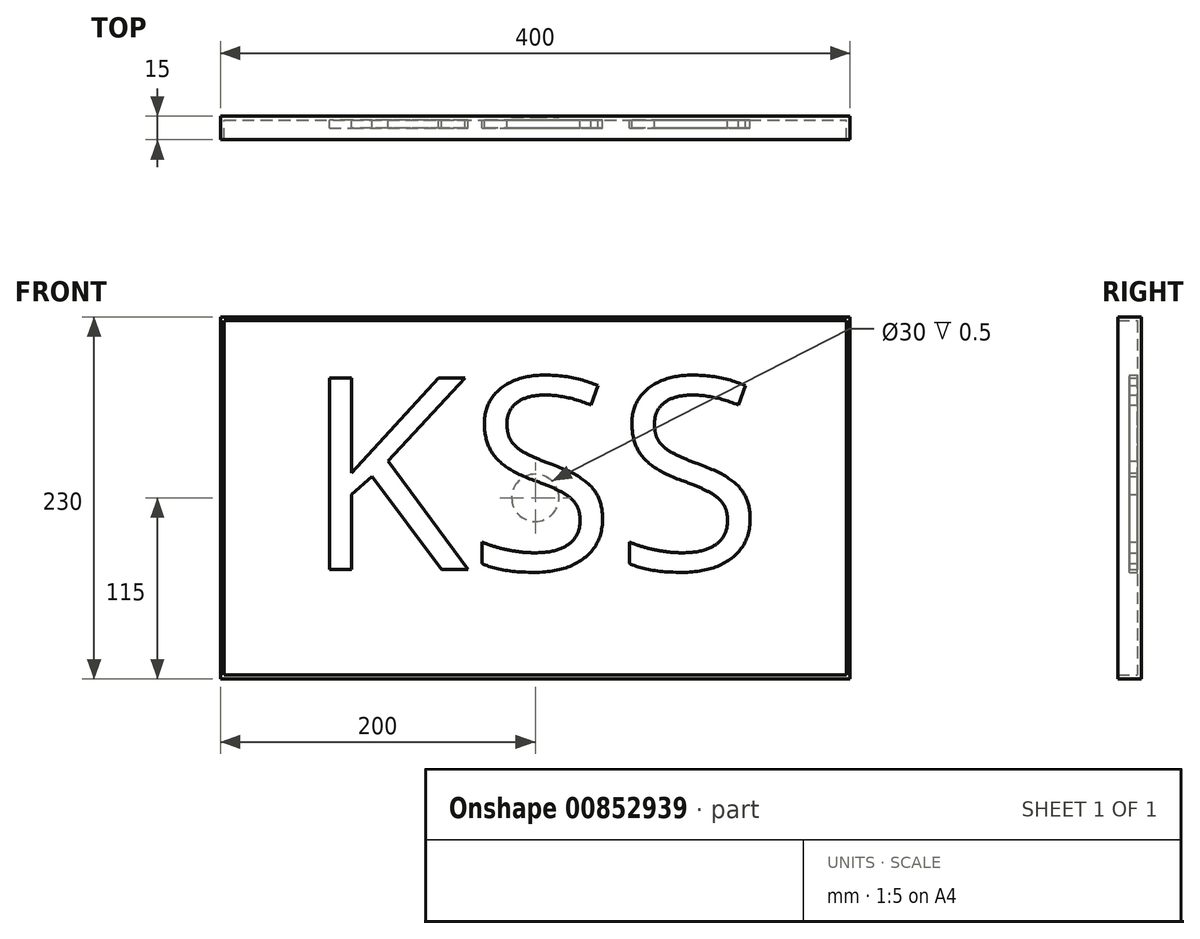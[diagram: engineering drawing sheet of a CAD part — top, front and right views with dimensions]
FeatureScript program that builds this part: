
annotation { "Feature Type Name" : "Feature", "Feature Type Description" : "" }
export const myFeature = defineFeature(function(context is Context, id is Id, definition is map)
    precondition{}
    {
        {
            var Q0;
            Q0=qCreatedBy(makeId("Front.planeOp"),FACE);
            var sketch = newSketch(context, id + "F0", { "sketchPlane" : qUnion([Q0])});
            skLineSegment(sketch, "E0.bottom", {"start": v(-200, 115) * mm, "end": v(200, 115) * mm});
            skLineSegment(sketch, "E0.top", {"start": v(-200, -115) * mm, "end": v(200, -115) * mm});
            skLineSegment(sketch, "E0.left", {"start": v(-200, 115) * mm, "end": v(-200, -115) * mm});
            skLineSegment(sketch, "E0.right", {"start": v(200, 115) * mm, "end": v(200, -115) * mm});
            skSolve(sketch);
        }
        {
            var Q0;
            Q0=makeQuery(id+"F0.imprint","IMPRINT",FACE,{"disambiguationData":[TD([[makeQuery(id+"F0.imprint","IMPRINT",EDGE,{"derivedFrom":sQuery(id+"F0.wireOp",EDGE,"E0.bottom")}),-1.0]])]});
            extrude(context, id + "F1", {"entities" : qUnion([Q0]), "depth" : 15 * mm, "offsetDistance" : 25 * mm});
        }
        {
            var Q0;
            Q0=makeQuery(id+"F1.opExtrude","CAP_FACE",FACE,{"disambiguationData":[OSD([sQuery(id+"F0.wireOp",EDGE,"E0.bottom"),sQuery(id+"F0.wireOp",EDGE,"E0.top"),sQuery(id+"F0.wireOp",EDGE,"E0.left"),sQuery(id+"F0.wireOp",EDGE,"E0.right")])],"isStart":false});
            shell(context, id + "F2", {"entities" : qUnion([Q0]), "thickness" : 2.5 * mm});
        }
        {
            var Q0;
            Q0=makeQuery(id+"F1.opExtrude","CAP_FACE",FACE,{"disambiguationData":[OSD([sQuery(id+"F0.wireOp",EDGE,"E0.bottom"),sQuery(id+"F0.wireOp",EDGE,"E0.top"),sQuery(id+"F0.wireOp",EDGE,"E0.left"),sQuery(id+"F0.wireOp",EDGE,"E0.right")])],"isStart":true});
            var sketch = newSketch(context, id + "F3", { "sketchPlane" : qUnion([Q0])});
            skCircle(sketch, "E1", {"center": v(0, 0) * mm, "radius": 15 * mm});
            skSolve(sketch);
        }
        {
            var Q0;
            Q0=makeQuery(id+"F3.imprint","IMPRINT",FACE,{"disambiguationData":[TD([[makeQuery(id+"F3.imprint","IMPRINT",EDGE,{"derivedFrom":sQuery(id+"F3.wireOp",EDGE,"E1")}),1.0]])]});
            extrude(context, id + "F4", {"entities" : qUnion([Q0]), "operationType" : NewBodyOperationType.REMOVE, "oppositeDirection" : true, "depth" : 0.5 * mm, "offsetDistance" : 25 * mm});
        }
        {
            var Q0;
            Q0=makeQuery(id+"F2.opShell","OFFSET_FACE",FACE,{"disambiguationData":[OSD([sQuery(id+"F0.wireOp",EDGE,"E0.bottom"),sQuery(id+"F0.wireOp",EDGE,"E0.top"),sQuery(id+"F0.wireOp",EDGE,"E0.left"),sQuery(id+"F0.wireOp",EDGE,"E0.right")])]});
            var sketch = newSketch(context, id + "F5", { "sketchPlane" : qUnion([Q0])});
            skText(sketch, "E2", { "text": "KSS\n", "fontName": "OpenSans-Regular.ttf"});
            const initialGuessF5  = {"E2": [-0.1475, -0.04564, 1, 0, 0.12289]};
            skSetInitialGuess(sketch, initialGuessF5);
            skSolve(sketch);
        }
        {
            var Q0;
            Q0=makeQuery(id+"F5.imprint","IMPRINT",FACE,{"disambiguationData":[TD([[makeQuery(id+"F5.imprint","IMPRINT",EDGE,{"derivedFrom":sQuery(id+"F5.wireOp",EDGE,"E2.sketch_text.stroke-0")}),-1.0]])]});
            var Q1;
            Q1 = qSketchRegion(id + "F5", true);
            extrude(context, id + "F6", {"entities" : qUnion([Q0, Q1]), "operationType" : NewBodyOperationType.ADD, "depth" : 5 * mm, "offsetDistance" : 25 * mm});
        }
    });
